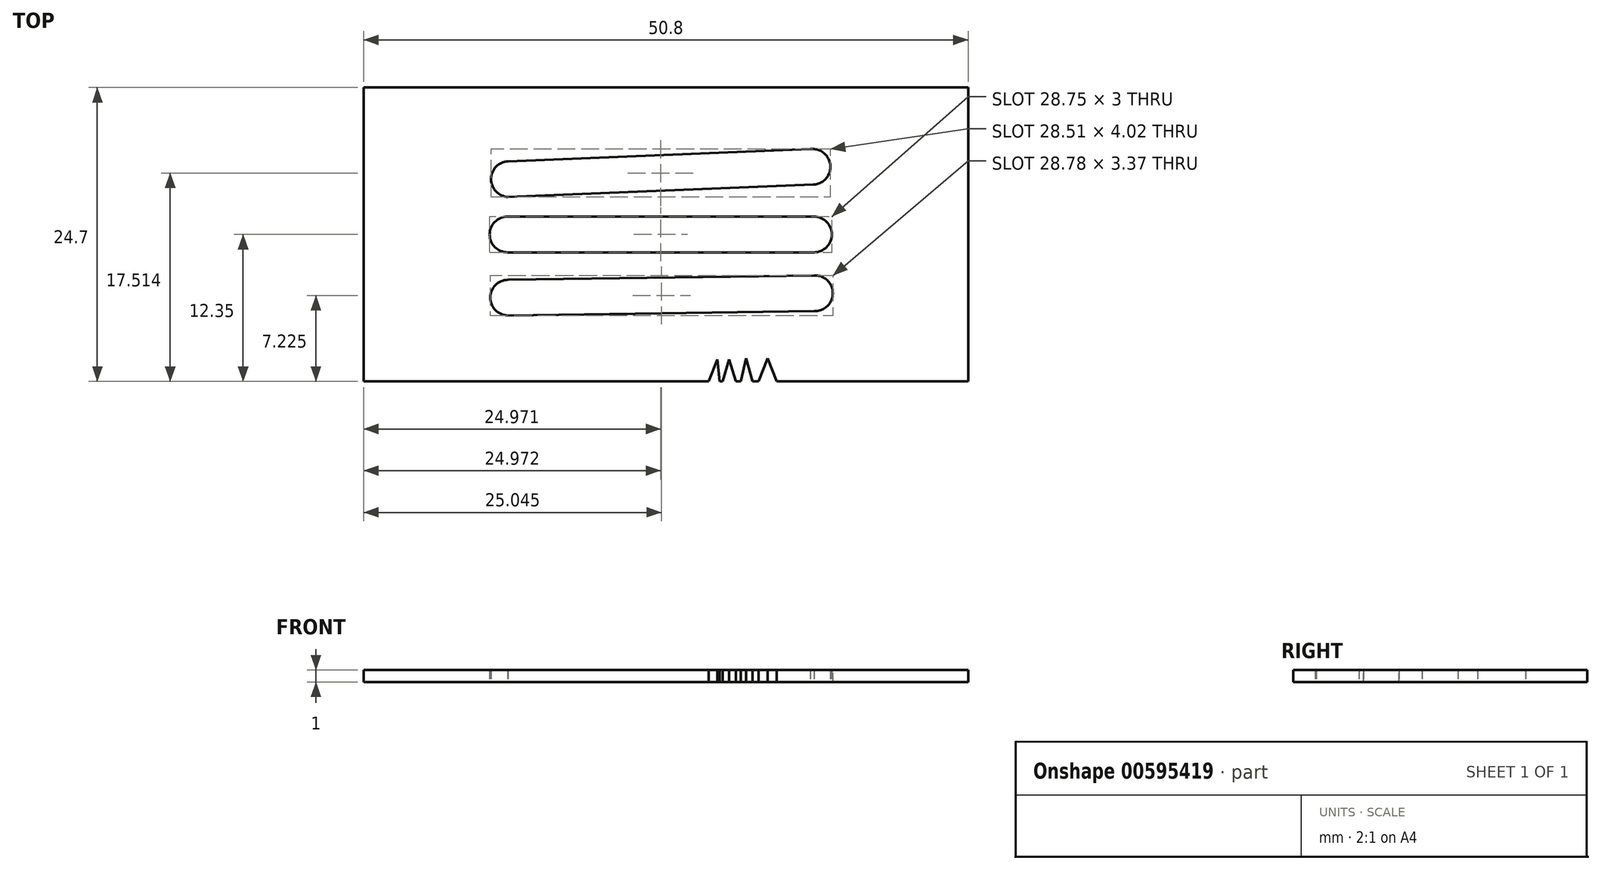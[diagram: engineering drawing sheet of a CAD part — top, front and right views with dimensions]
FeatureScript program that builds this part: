
annotation { "Feature Type Name" : "Feature", "Feature Type Description" : "" }
export const myFeature = defineFeature(function(context is Context, id is Id, definition is map)
    precondition{}
    {
        {
            var Q0;
            Q0=qCreatedBy(makeId("Top.planeOp"),FACE);
            var sketch = newSketch(context, id + "F0", { "sketchPlane" : qUnion([Q0])});
            skLineSegment(sketch, "E0.bottom", {"start": v(25.4, 12.35) * mm, "end": v(-25.4, 12.35) * mm});
            skLineSegment(sketch, "E0.top", {"start": v(25.4, -12.35) * mm, "end": v(-25.4, -12.35) * mm});
            skLineSegment(sketch, "E0.left", {"start": v(25.4, 12.35) * mm, "end": v(25.4, -12.35) * mm});
            skLineSegment(sketch, "E0.right", {"start": v(-25.4, 12.35) * mm, "end": v(-25.4, -12.35) * mm});
            skPoint(sketch, "E0.middle", {"position": v(0, 0) * mm});
            skSolve(sketch);
        }
        {
            var Q0;
            Q0 = qSketchRegion(id + "F0", true);
            extrude(context, id + "F1", {"entities" : qUnion([Q0]), "endBound" : BoundingType.SYMMETRIC, "depth" : 1 * mm, "offsetDistance" : 25 * mm});
        }
        {
            var Q0;
            Q0=makeQuery(id+"F1.opExtrude","CAP_FACE",FACE,{"disambiguationData":[OSD([sQuery(id+"F0.wireOp",EDGE,"E0.bottom"),sQuery(id+"F0.wireOp",EDGE,"E0.top"),sQuery(id+"F0.wireOp",EDGE,"E0.left"),sQuery(id+"F0.wireOp",EDGE,"E0.right")])],"isStart":false});
            var sketch = newSketch(context, id + "F2", { "sketchPlane" : qUnion([Q0])});
            skCircle(sketch, "E1", {"center": v(12.53, -4.94) * mm, "radius": 1.5 * mm});
            skSolve(sketch);
        }
        {
            var Q0;
            Q0 = qSketchRegion(id + "F2", true);
            extrude(context, id + "F3", {"entities" : qUnion([Q0]), "operationType" : NewBodyOperationType.REMOVE, "oppositeDirection" : true, "depth" : 25 * mm, "offsetDistance" : 25 * mm});
        }
        {
            var Q0;
            Q0=makeQuery(id+"F1.opExtrude","CAP_FACE",FACE,{"disambiguationData":[OSD([sQuery(id+"F0.wireOp",EDGE,"E0.bottom"),sQuery(id+"F0.wireOp",EDGE,"E0.top"),sQuery(id+"F0.wireOp",EDGE,"E0.left"),sQuery(id+"F0.wireOp",EDGE,"E0.right")])],"isStart":true});
            var sketch = newSketch(context, id + "F4", { "sketchPlane" : qUnion([Q0])});
            skCircle(sketch, "E2", {"center": v(-13.25, 5.31) * mm, "radius": 1.5 * mm});
            skCircle(sketch, "E3", {"center": v(12.45, 0) * mm, "radius": 1.5 * mm});
            skCircle(sketch, "E4", {"center": v(-13.3, 0) * mm, "radius": 1.5 * mm});
            skCircle(sketch, "E5", {"center": v(12.33, -5.68) * mm, "radius": 1.5 * mm});
            skCircle(sketch, "E6", {"center": v(-13.18, -4.65) * mm, "radius": 1.5 * mm});
            skLineSegment(sketch, "E7", {"start": v(12.16, -7.17) * mm, "end": v(-13.24, -6.15) * mm});
            skLineSegment(sketch, "E8", {"start": v(-13.24, -6.15) * mm, "end": v(-13.24, -3.15) * mm});
            skLineSegment(sketch, "E9", {"start": v(-13.24, -3.15) * mm, "end": v(12.39, -4.19) * mm});
            skLineSegment(sketch, "E10", {"start": v(12.39, -4.19) * mm, "end": v(12.16, -7.17) * mm});
            skLineSegment(sketch, "E11", {"start": v(12.45, -1.5) * mm, "end": v(-13.3, -1.5) * mm});
            skLineSegment(sketch, "E12", {"start": v(-13.3, -1.5) * mm, "end": v(-13.3, 1.5) * mm});
            skLineSegment(sketch, "E13", {"start": v(-13.3, 1.5) * mm, "end": v(12.45, 1.5) * mm});
            skLineSegment(sketch, "E14", {"start": v(12.45, 1.5) * mm, "end": v(12.45, -1.5) * mm});
            skLineSegment(sketch, "E15", {"start": v(12.45, 3.44) * mm, "end": v(-13.3, 3.81) * mm});
            skLineSegment(sketch, "E16", {"start": v(-13.3, 3.81) * mm, "end": v(-13.25, 5.31) * mm});
            skLineSegment(sketch, "E17", {"start": v(-13.3, 6.8) * mm, "end": v(-13.25, 5.31) * mm});
            skLineSegment(sketch, "E18", {"start": v(12.45, 6.44) * mm, "end": v(-13.3, 6.8) * mm});
            skLineSegment(sketch, "E19", {"start": v(12.45, 6.44) * mm, "end": v(12.45, 3.44) * mm});
            skSolve(sketch);
        }
        {
            var Q0;
            {var subQ0=sQuery(id+"F4.wireOp",EDGE,"E17");Q0=makeQuery(id+"F4.imprint","IMPRINT",FACE,{"disambiguationData":[TD([[makeQuery(id+"F4.imprint","IMPRINT",EDGE,{"derivedFrom":subQ0}),1.0]])]});}
            var Q1;
            {var subQ0=sQuery(id+"F4.wireOp",EDGE,"E17");Q1=makeQuery(id+"F4.imprint","IMPRINT",FACE,{"disambiguationData":[TD([[makeQuery(id+"F4.imprint","IMPRINT",EDGE,{"derivedFrom":subQ0}),-1.0]])]});}
            extrude(context, id + "F5", {"entities" : qUnion([Q0, Q1]), "operationType" : NewBodyOperationType.REMOVE, "oppositeDirection" : true, "depth" : 25 * mm, "offsetDistance" : 25 * mm});
        }
        {
            var Q0;
            {var subQ0=sQuery(id+"F4.wireOp",EDGE,"E18");var subQ1=sQuery(id+"F4.wireOp",EDGE,"E2");var subQ2=makeQuery(id+"F4.imprint","INTERSECT",VERTEX,{"derivedFrom":[subQ1,subQ0]});Q0=makeQuery(id+"F4.imprint","IMPRINT",FACE,{"disambiguationData":[TD([[makeQuery(id+"F4.imprint","IMPRINT",EDGE,{"disambiguationData":[TD([[subQ2,1.0]])],"derivedFrom":subQ1}),-1.0]])]});}
            extrude(context, id + "F6", {"entities" : qUnion([Q0]), "operationType" : NewBodyOperationType.REMOVE, "oppositeDirection" : true, "depth" : 25 * mm, "offsetDistance" : 25 * mm});
        }
        {
            var Q0;
            {var subQ0=sQuery(id+"F4.wireOp",EDGE,"E14");Q0=makeQuery(id+"F4.imprint","IMPRINT",FACE,{"disambiguationData":[TD([[makeQuery(id+"F4.imprint","IMPRINT",EDGE,{"derivedFrom":subQ0}),1.0]])]});}
            var Q1;
            {var subQ0=sQuery(id+"F4.wireOp",EDGE,"E14");Q1=makeQuery(id+"F4.imprint","IMPRINT",FACE,{"disambiguationData":[TD([[makeQuery(id+"F4.imprint","IMPRINT",EDGE,{"derivedFrom":subQ0}),-1.0]])]});}
            var Q2;
            {var subQ1=sQuery(id+"F4.wireOp",EDGE,"E11");Q2=makeQuery(id+"F4.imprint","IMPRINT",FACE,{"disambiguationData":[TD([[makeQuery(id+"F4.imprint","IMPRINT",EDGE,{"derivedFrom":subQ1}),-1.0]])]});}
            var Q3;
            {var subQ0=sQuery(id+"F4.wireOp",EDGE,"E12");Q3=makeQuery(id+"F4.imprint","IMPRINT",FACE,{"disambiguationData":[TD([[makeQuery(id+"F4.imprint","IMPRINT",EDGE,{"derivedFrom":subQ0}),-1.0]])]});}
            var Q4;
            {var subQ0=sQuery(id+"F4.wireOp",EDGE,"E12");Q4=makeQuery(id+"F4.imprint","IMPRINT",FACE,{"disambiguationData":[TD([[makeQuery(id+"F4.imprint","IMPRINT",EDGE,{"derivedFrom":subQ0}),1.0]])]});}
            var Q5;
            {var subQ0=sQuery(id+"F4.wireOp",EDGE,"E10");Q5=makeQuery(id+"F4.imprint","IMPRINT",FACE,{"disambiguationData":[TD([[makeQuery(id+"F4.imprint","IMPRINT",EDGE,{"derivedFrom":subQ0}),1.0]])]});}
            var Q6;
            {var subQ0=sQuery(id+"F4.wireOp",EDGE,"E10");Q6=makeQuery(id+"F4.imprint","IMPRINT",FACE,{"disambiguationData":[TD([[makeQuery(id+"F4.imprint","IMPRINT",EDGE,{"derivedFrom":subQ0}),-1.0]])]});}
            var Q7;
            {var subQ1=sQuery(id+"F4.wireOp",EDGE,"E7");Q7=makeQuery(id+"F4.imprint","IMPRINT",FACE,{"disambiguationData":[TD([[makeQuery(id+"F4.imprint","IMPRINT",EDGE,{"derivedFrom":subQ1}),-1.0]])]});}
            var Q8;
            {var subQ0=sQuery(id+"F4.wireOp",EDGE,"E8");Q8=makeQuery(id+"F4.imprint","IMPRINT",FACE,{"disambiguationData":[TD([[makeQuery(id+"F4.imprint","IMPRINT",EDGE,{"derivedFrom":subQ0}),-1.0]])]});}
            var Q9;
            {var subQ0=sQuery(id+"F4.wireOp",EDGE,"E8");Q9=makeQuery(id+"F4.imprint","IMPRINT",FACE,{"disambiguationData":[TD([[makeQuery(id+"F4.imprint","IMPRINT",EDGE,{"derivedFrom":subQ0}),1.0]])]});}
            extrude(context, id + "F7", {"entities" : qUnion([Q0, Q1, Q2, Q3, Q4, Q5, Q6, Q7, Q8, Q9]), "operationType" : NewBodyOperationType.REMOVE, "oppositeDirection" : true, "depth" : 25 * mm, "offsetDistance" : 25 * mm});
        }
        {
            var Q0;
            {var subQ1=sQuery(id+"F4.wireOp",EDGE,"E7");Q0=makeQuery(id+"F4.imprint","IMPRINT",FACE,{"disambiguationData":[TD([[makeQuery(id+"F4.imprint","IMPRINT",EDGE,{"derivedFrom":subQ1}),1.0]])]});}
            var sketch = newSketch(context, id + "F8", { "sketchPlane" : qUnion([Q0])});
            skLineSegment(sketch, "E20", {"start": v(9.33, 12.35) * mm, "end": v(8.56, 10.4) * mm});
            skLineSegment(sketch, "E21", {"start": v(8.56, 10.4) * mm, "end": v(7.5, 13.08) * mm});
            skLineSegment(sketch, "E22", {"start": v(7.5, 13.08) * mm, "end": v(6.75, 10.4) * mm});
            skLineSegment(sketch, "E23", {"start": v(6.75, 10.4) * mm, "end": v(6.11, 13.08) * mm});
            skLineSegment(sketch, "E24", {"start": v(6.11, 13.08) * mm, "end": v(5.32, 10.5) * mm});
            skLineSegment(sketch, "E25", {"start": v(5.32, 10.5) * mm, "end": v(4.57, 13.08) * mm});
            skLineSegment(sketch, "E26", {"start": v(4.57, 13.08) * mm, "end": v(4.34, 10.5) * mm});
            skLineSegment(sketch, "E27", {"start": v(4.34, 10.5) * mm, "end": v(3.27, 13.19) * mm});
            skLineSegment(sketch, "E28", {"start": v(3.27, 13.19) * mm, "end": v(9.33, 12.35) * mm});
            skSolve(sketch);
        }
        {
            var Q0;
            {var subQ0=sQuery(id+"F8.wireOp",EDGE,"E20");Q0=makeQuery(id+"F8.imprint","IMPRINT",FACE,{"disambiguationData":[TD([[makeQuery(id+"F8.imprint","IMPRINT",EDGE,{"derivedFrom":subQ0}),-1.0]])]});}
            var Q1;
            {var subQ0=sQuery(id+"F8.wireOp",EDGE,"E23");var subQ1=sQuery(id+"F8.wireOp",EDGE,"E22");var subQ2=makeQuery(id+"F8.imprint","INTERSECT",VERTEX,{"derivedFrom":[subQ1,subQ0]});Q1=makeQuery(id+"F8.imprint","IMPRINT",FACE,{"disambiguationData":[TD([[makeQuery(id+"F8.imprint","IMPRINT",EDGE,{"disambiguationData":[TD([[subQ2,1.0]])],"derivedFrom":subQ1}),-1.0]])]});}
            var Q2;
            {var subQ0=sQuery(id+"F8.wireOp",EDGE,"E25");var subQ1=sQuery(id+"F8.wireOp",EDGE,"E24");var subQ2=makeQuery(id+"F8.imprint","INTERSECT",VERTEX,{"derivedFrom":[subQ1,subQ0]});Q2=makeQuery(id+"F8.imprint","IMPRINT",FACE,{"disambiguationData":[TD([[makeQuery(id+"F8.imprint","IMPRINT",EDGE,{"disambiguationData":[TD([[subQ2,1.0]])],"derivedFrom":subQ1}),-1.0]])]});}
            var Q3;
            {var subQ0=sQuery(id+"F8.wireOp",EDGE,"E27");var subQ1=sQuery(id+"F8.wireOp",EDGE,"E26");var subQ2=makeQuery(id+"F8.imprint","INTERSECT",VERTEX,{"derivedFrom":[subQ1,subQ0]});Q3=makeQuery(id+"F8.imprint","IMPRINT",FACE,{"disambiguationData":[TD([[makeQuery(id+"F8.imprint","IMPRINT",EDGE,{"disambiguationData":[TD([[subQ2,1.0]])],"derivedFrom":subQ1}),-1.0]])]});}
            extrude(context, id + "F9", {"entities" : qUnion([Q0, Q1, Q2, Q3]), "operationType" : NewBodyOperationType.REMOVE, "oppositeDirection" : true, "depth" : 25 * mm, "offsetDistance" : 25 * mm});
        }
    });
